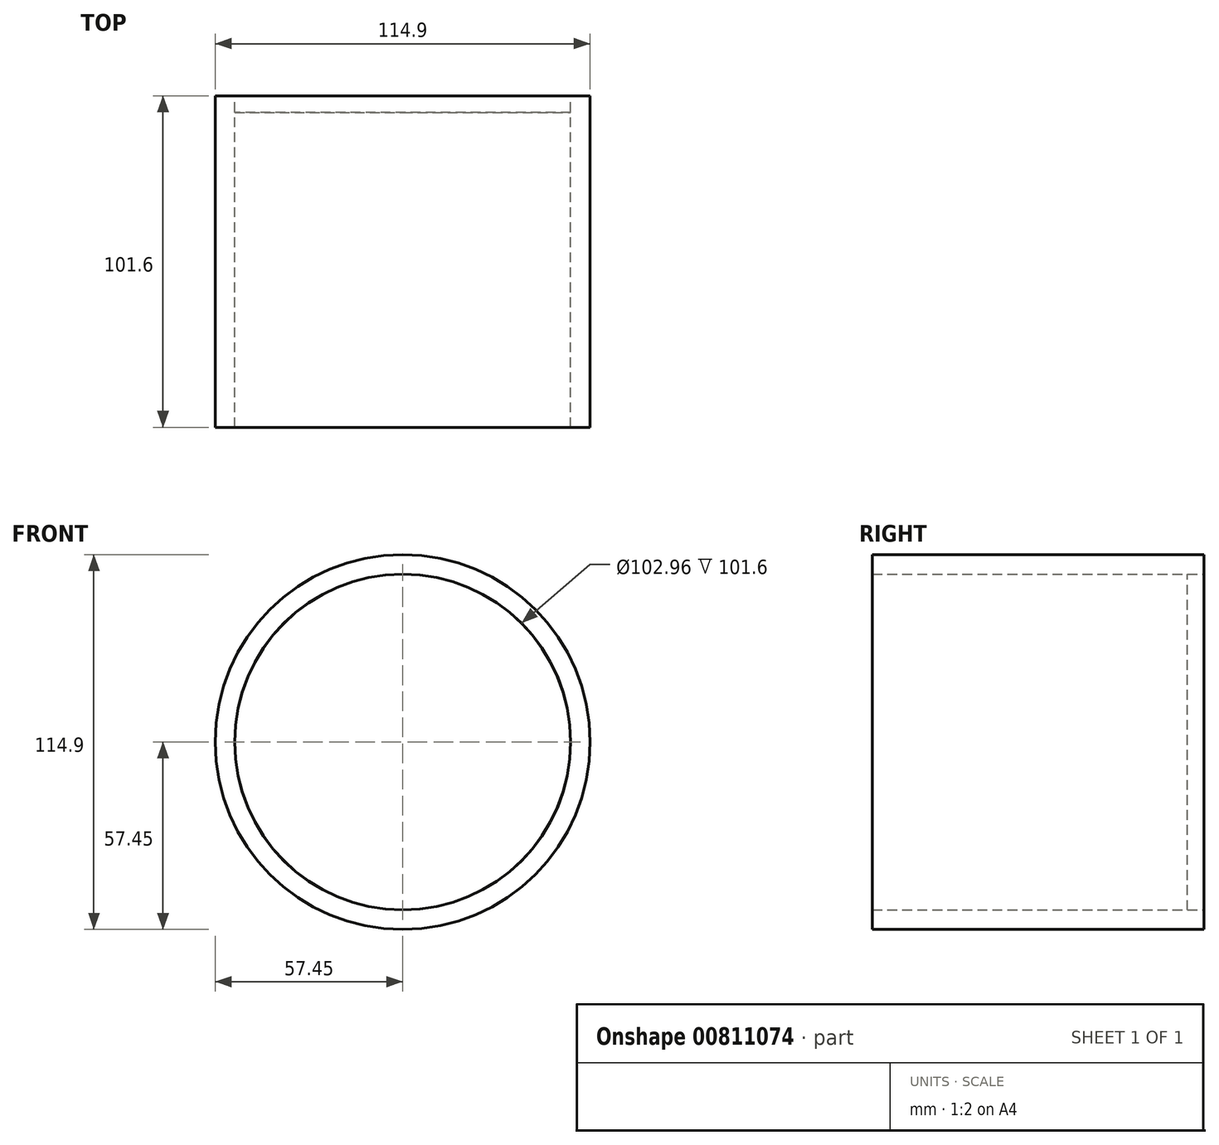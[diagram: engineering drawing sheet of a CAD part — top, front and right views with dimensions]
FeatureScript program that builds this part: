
annotation { "Feature Type Name" : "Feature", "Feature Type Description" : "" }
export const myFeature = defineFeature(function(context is Context, id is Id, definition is map)
    precondition{}
    {
        {
            var Q0;
            Q0=qCreatedBy(makeId("Front.planeOp"),FACE);
            var sketch = newSketch(context, id + "F0", { "sketchPlane" : qUnion([Q0])});
            skCircle(sketch, "E0", {"center": v(0, 0) * mm, "radius": 57.45 * mm});
            skCircle(sketch, "E1", {"center": v(0, 0) * mm, "radius": 51.48 * mm});
            skSolve(sketch);
        }
        {
            var Q0;
            Q0=makeQuery(id+"F0.imprint","IMPRINT",FACE,{"disambiguationData":[TD([[makeQuery(id+"F0.imprint","IMPRINT",EDGE,{"derivedFrom":sQuery(id+"F0.wireOp",EDGE,"E1")}),-1.0]])]});
            extrude(context, id + "F1", {"entities" : qUnion([Q0]), "depth" : 101.6 * mm, "offsetDistance" : 25.4 * mm});
        }
        {
            var Q0;
            Q0=makeQuery(id+"F0.imprint","IMPRINT",FACE,{"disambiguationData":[TD([[makeQuery(id+"F0.imprint","IMPRINT",EDGE,{"derivedFrom":sQuery(id+"F0.wireOp",EDGE,"E1")}),1.0]])]});
            var sketch = newSketch(context, id + "F2", { "sketchPlane" : qUnion([Q0])});
            skCircle(sketch, "E2", {"center": v(0, 0) * mm, "radius": 51.45 * mm});
            skSolve(sketch);
        }
        {
            var Q0;
            Q0 = qSketchRegion(id + "F2", true);
            extrude(context, id + "F3", {"entities" : qUnion([Q0]), "depth" : 5.08 * mm, "offsetDistance" : 25.4 * mm});
        }
    });
